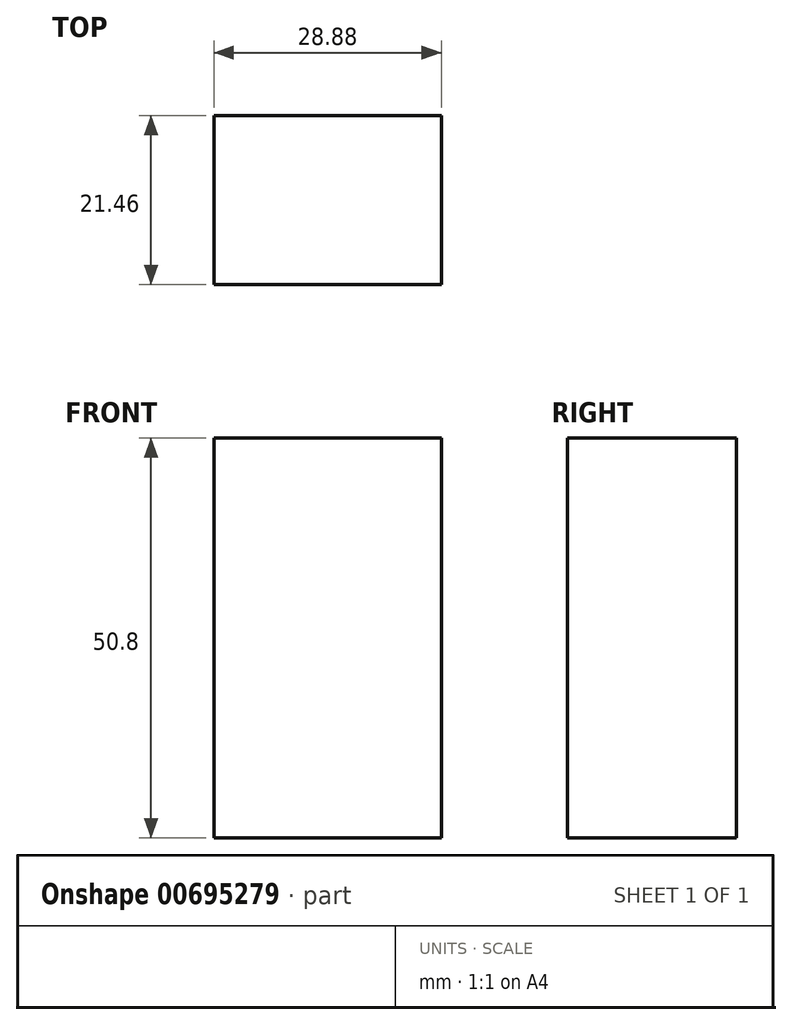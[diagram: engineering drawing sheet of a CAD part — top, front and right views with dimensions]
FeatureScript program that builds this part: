
annotation { "Feature Type Name" : "Feature", "Feature Type Description" : "" }
export const myFeature = defineFeature(function(context is Context, id is Id, definition is map)
    precondition{}
    {
        {
            var Q0;
            Q0=qCreatedBy(makeId("Top.planeOp"),FACE);
            var sketch = newSketch(context, id + "F0", { "sketchPlane" : qUnion([Q0])});
            skLineSegment(sketch, "E0.bottom", {"start": v(-47.3, -53.58) * mm, "end": v(-18.41, -53.58) * mm});
            skLineSegment(sketch, "E0.top", {"start": v(-47.3, -32.12) * mm, "end": v(-18.41, -32.12) * mm});
            skLineSegment(sketch, "E0.left", {"start": v(-47.3, -53.58) * mm, "end": v(-47.3, -32.12) * mm});
            skLineSegment(sketch, "E0.right", {"start": v(-18.41, -53.58) * mm, "end": v(-18.41, -32.12) * mm});
            skSolve(sketch);
        }
        {
            var Q0;
            Q0=makeQuery(id+"F0.imprint","IMPRINT",FACE,{"disambiguationData":[TD([[makeQuery(id+"F0.imprint","IMPRINT",EDGE,{"derivedFrom":sQuery(id+"F0.wireOp",EDGE,"E0.bottom")}),1.0]])]});
            extrude(context, id + "F1", {"entities" : qUnion([Q0]), "depth" : 50.8 * mm, "offsetDistance" : 25.4 * mm});
        }
    });
